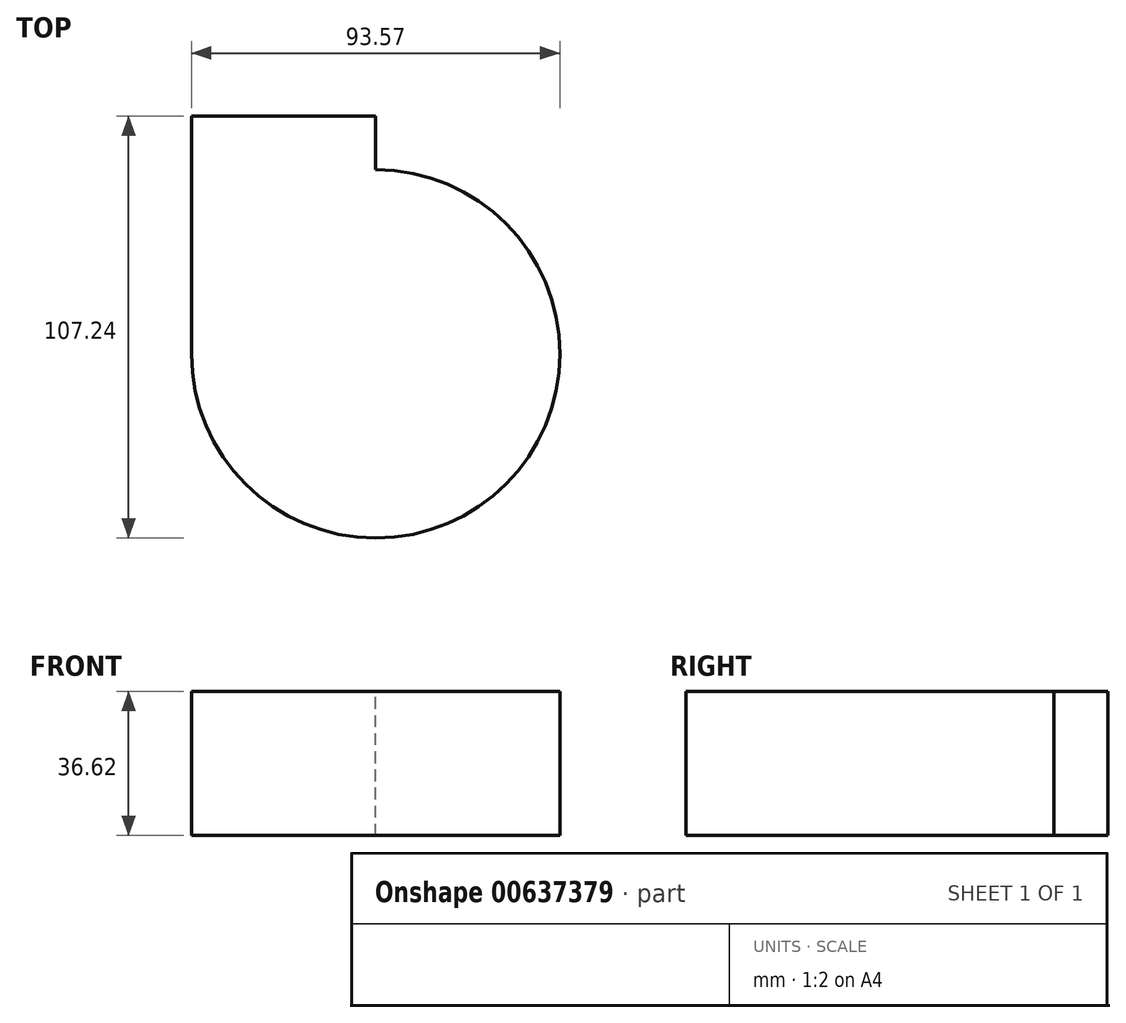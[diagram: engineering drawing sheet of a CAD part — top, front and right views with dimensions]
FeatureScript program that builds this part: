
annotation { "Feature Type Name" : "Feature", "Feature Type Description" : "" }
export const myFeature = defineFeature(function(context is Context, id is Id, definition is map)
    precondition{}
    {
        {
            var Q0;
            Q0=qCreatedBy(makeId("Front.planeOp"),FACE);
            var sketch = newSketch(context, id + "F0", { "sketchPlane" : qUnion([Q0])});
            skLineSegment(sketch, "E0.bottom", {"start": v(0, 36.62) * mm, "end": v(46.79, 36.62) * mm});
            skLineSegment(sketch, "E0.top", {"start": v(0, 0) * mm, "end": v(46.79, 0) * mm});
            skLineSegment(sketch, "E0.left", {"start": v(0, 36.62) * mm, "end": v(0, 0) * mm});
            skLineSegment(sketch, "E0.right", {"start": v(46.79, 36.62) * mm, "end": v(46.79, 0) * mm});
            skSolve(sketch);
        }
        {
            var Q0;
            Q0=makeQuery(id+"F0.imprint","IMPRINT",FACE,{"disambiguationData":[TD([[makeQuery(id+"F0.imprint","IMPRINT",EDGE,{"derivedFrom":sQuery(id+"F0.wireOp",EDGE,"E0.bottom")}),-1.0]])]});
            extrude(context, id + "F1", {"entities" : qUnion([Q0]), "depth" : 60.45 * mm, "offsetDistance" : 25.4 * mm});
        }
        {
            var Q0;
            Q0=makeQuery(id+"F1.opExtrude","CAP_FACE",FACE,{"disambiguationData":[OSD([sQuery(id+"F0.wireOp",EDGE,"E0.bottom"),sQuery(id+"F0.wireOp",EDGE,"E0.top"),sQuery(id+"F0.wireOp",EDGE,"E0.left"),sQuery(id+"F0.wireOp",EDGE,"E0.right")])],"isStart":false});
            var Q1;
            Q1=makeQuery(id+"F1.opExtrude","CAP_EDGE",EDGE,{"disambiguationData":[OSD([sQuery(id+"F0.wireOp",EDGE,"E0.right")])],"isStart":false});
            revolve(context, id + "F2", {"operationType" : NewBodyOperationType.ADD, "entities" : qUnion([Q0]), "axis" : qUnion([Q1]), "revolveType" : RevolveType.FULL});
        }
    });
